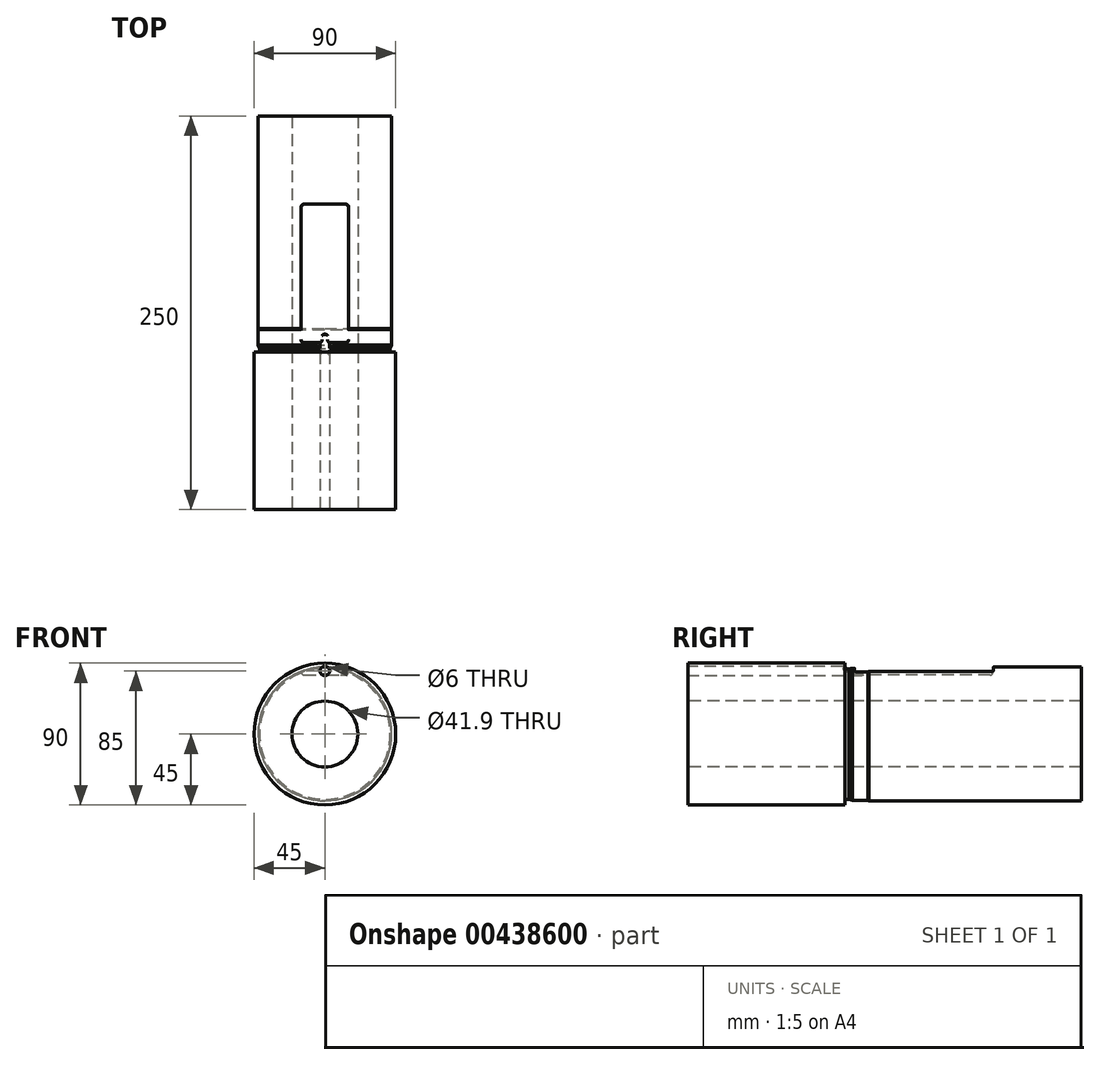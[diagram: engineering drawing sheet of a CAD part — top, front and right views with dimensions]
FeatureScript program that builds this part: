
annotation { "Feature Type Name" : "Feature", "Feature Type Description" : "" }
export const myFeature = defineFeature(function(context is Context, id is Id, definition is map)
    precondition{}
    {
        {
            var Q0;
            Q0=qCreatedBy(makeId("Right.planeOp"),FACE);
            var sketch = newSketch(context, id + "F0", { "sketchPlane" : qUnion([Q0])});
            skLineSegment(sketch, "E0", {"start": v(-100, 20.95) * mm, "end": v(-100, 45) * mm});
            skLineSegment(sketch, "E1", {"start": v(-100, 45) * mm, "end": v(0, 45) * mm});
            skLineSegment(sketch, "E2", {"start": v(0, 45) * mm, "end": v(0, 42.8) * mm});
            skArc(sketch, "E3", {"start": v(0, 42.8) * mm, "mid": v(0.38, 41.88) * mm, "end": v(1.3, 41.5) * mm});
            skLineSegment(sketch, "E4", {"start": v(4.63, 42.27) * mm, "end": v(14.4, 42.27) * mm});
            skLineSegment(sketch, "E5", {"start": v(14.4, 42.27) * mm, "end": v(15.2, 42.5) * mm});
            skLineSegment(sketch, "E6", {"start": v(15.2, 42.5) * mm, "end": v(150, 42.5) * mm});
            skLineSegment(sketch, "E7", {"start": v(150, 42.49) * mm, "end": v(150, 20.95) * mm});
            skLineSegment(sketch, "E8", {"start": v(-123.16, 0) * mm, "end": v(120.4, 0) * mm, "construction": true});
            skLineSegment(sketch, "E9", {"start": v(1.3, 41.5) * mm, "end": v(2.5, 41.5) * mm});
            skLineSegment(sketch, "E10", {"start": v(2.5, 41.5) * mm, "end": v(4.63, 42.27) * mm});
            skLineSegment(sketch, "E11", {"start": v(-100, 20.95) * mm, "end": v(150, 20.95) * mm});
            skSolve(sketch);
        }
        {
            var Q0;
            Q0=makeQuery(id+"F0.imprint","IMPRINT",FACE,{"disambiguationData":[TD([[makeQuery(id+"F0.imprint","IMPRINT",EDGE,{"derivedFrom":sQuery(id+"F0.wireOp",EDGE,"E0")}),-1.0]])]});
            var Q1;
            Q1=sQuery(id+"F0.wireOp",EDGE,"E8");
            revolve(context, id + "F1", {"entities" : qUnion([Q0]), "axis" : qUnion([Q1]), "revolveType" : RevolveType.FULL});
        }
        {
            var Q0;
            Q0=makeQuery(id+"F1.opRevolve","SWEPT_FACE",FACE,{"disambiguationData":[OSD([sQuery(id+"F0.wireOp",EDGE,"E0")])]});
            var sketch = newSketch(context, id + "F2", { "sketchPlane" : qUnion([Q0])});
            skCircle(sketch, "E12", {"center": v(0, 40) * mm, "radius": 3 * mm});
            skSolve(sketch);
        }
        {
            var Q0;
            Q0 = qSketchRegion(id + "F2", true);
            extrude(context, id + "F3", {"entities" : qUnion([Q0]), "operationType" : NewBodyOperationType.REMOVE, "oppositeDirection" : true, "depth" : 111.5 * mm, "offsetDistance" : 25 * mm});
        }
        {
            var Q0;
            Q0=qCreatedBy(makeId("Right.planeOp"),FACE);
            var sketch = newSketch(context, id + "F4", { "sketchPlane" : qUnion([Q0])});
            skLineSegment(sketch, "E13", {"start": v(94, 42.5) * mm, "end": v(94, 37.5) * mm});
            skLineSegment(sketch, "E14", {"start": v(94, 37.5) * mm, "end": v(6, 37.5) * mm});
            skLineSegment(sketch, "E15", {"start": v(6, 37.5) * mm, "end": v(6, 42.5) * mm});
            skLineSegment(sketch, "E16", {"start": v(6, 42.5) * mm, "end": v(94, 42.5) * mm});
            skSolve(sketch);
        }
        {
            var Q0;
            Q0 = qSketchRegion(id + "F4", true);
            extrude(context, id + "F5", {"entities" : qUnion([Q0]), "operationType" : NewBodyOperationType.REMOVE, "endBound" : BoundingType.SYMMETRIC, "oppositeDirection" : true, "depth" : 30 * mm, "offsetDistance" : 25 * mm});
        }
        {
            var Q0;
            Q0=qCreatedBy(makeId("Right.planeOp"),FACE);
            var sketch = newSketch(context, id + "F6", { "sketchPlane" : qUnion([Q0])});
            skLineSegment(sketch, "E17.bottom", {"start": v(2, 44.7) * mm, "end": v(8, 44.7) * mm});
            skLineSegment(sketch, "E17.top", {"start": v(2, 41.7) * mm, "end": v(8, 41.7) * mm});
            skLineSegment(sketch, "E17.left", {"start": v(2, 44.7) * mm, "end": v(2, 41.7) * mm});
            skLineSegment(sketch, "E17.right", {"start": v(8, 44.7) * mm, "end": v(8, 41.7) * mm});
            skSolve(sketch);
        }
        {
            var Q0;
            Q0 = qSketchRegion(id + "F6", true);
            extrude(context, id + "F7", {"entities" : qUnion([Q0]), "operationType" : NewBodyOperationType.REMOVE, "endBound" : BoundingType.SYMMETRIC, "oppositeDirection" : true, "depth" : 30 * mm, "offsetDistance" : 25 * mm});
        }
        {
            var Q0;
            Q0=makeQuery(id+"F5.boolean.opBoolean","COPY",EDGE,{"derivedFrom":makeQuery(id+"F5.opExtrude","CAP_EDGE",EDGE,{"disambiguationData":[OSD([sQuery(id+"F4.wireOp",EDGE,"E15")])],"isStart":false})});
            var Q1;
            Q1=makeQuery(id+"F5.boolean.opBoolean","COPY",EDGE,{"derivedFrom":makeQuery(id+"F5.opExtrude","CAP_EDGE",EDGE,{"disambiguationData":[OSD([sQuery(id+"F4.wireOp",EDGE,"E15")])],"isStart":true})});
            var Q2;
            Q2=makeQuery(id+"F5.boolean.opBoolean","COPY",EDGE,{"derivedFrom":makeQuery(id+"F5.opExtrude","CAP_EDGE",EDGE,{"disambiguationData":[OSD([sQuery(id+"F4.wireOp",EDGE,"E13")])],"isStart":true})});
            var Q3;
            Q3=makeQuery(id+"F5.boolean.opBoolean","COPY",EDGE,{"derivedFrom":makeQuery(id+"F5.opExtrude","CAP_EDGE",EDGE,{"disambiguationData":[OSD([sQuery(id+"F4.wireOp",EDGE,"E13")])],"isStart":false})});
            var Q4;
            Q4=makeQuery(id+"F5.boolean.opBoolean","COPY",EDGE,{"derivedFrom":makeQuery(id+"F5.opExtrude","SWEPT_EDGE",EDGE,{"disambiguationData":[OSD([sQuery(id+"F4.wireOp",EDGE,"E13"),sQuery(id+"F4.wireOp",EDGE,"E14")])]})});
            var Q5;
            Q5=makeQuery(id+"F5.boolean.opBoolean","COPY",EDGE,{"derivedFrom":makeQuery(id+"F5.opExtrude","CAP_EDGE",EDGE,{"disambiguationData":[OSD([sQuery(id+"F4.wireOp",EDGE,"E14")])],"isStart":false})});
            var Q6;
            Q6=makeQuery(id+"F5.boolean.opBoolean","COPY",EDGE,{"derivedFrom":makeQuery(id+"F5.opExtrude","CAP_EDGE",EDGE,{"disambiguationData":[OSD([sQuery(id+"F4.wireOp",EDGE,"E14")])],"isStart":true})});
            var Q7;
            {var subQ0=sQuery(id+"F4.wireOp",EDGE,"E15");var subQ1=sQuery(id+"F4.wireOp",EDGE,"E14");Q7=makeQuery(id+"F5.boolean.opBoolean","COPY",EDGE,{"disambiguationData":[TD([makeQuery(id+"F5.opExtrude","CAP_FACE",FACE,{"disambiguationData":[OSD([sQuery(id+"F4.wireOp",EDGE,"E13"),subQ1,subQ0,sQuery(id+"F4.wireOp",EDGE,"E16")])],"isStart":true})])],"derivedFrom":makeQuery(id+"F5.opExtrude","SWEPT_EDGE",EDGE,{"disambiguationData":[OSD([subQ1,subQ0])]})});}
            var Q8;
            {var subQ0=sQuery(id+"F4.wireOp",EDGE,"E15");var subQ1=sQuery(id+"F4.wireOp",EDGE,"E14");Q8=makeQuery(id+"F5.boolean.opBoolean","COPY",EDGE,{"disambiguationData":[TD([makeQuery(id+"F5.opExtrude","CAP_FACE",FACE,{"disambiguationData":[OSD([sQuery(id+"F4.wireOp",EDGE,"E13"),subQ1,subQ0,sQuery(id+"F4.wireOp",EDGE,"E16")])],"isStart":false})])],"derivedFrom":makeQuery(id+"F5.opExtrude","SWEPT_EDGE",EDGE,{"disambiguationData":[OSD([subQ1,subQ0])]})});}
            fillet(context, id + "F8", {"entities" : qUnion([Q0, Q1, Q2, Q3, Q4, Q5, Q6, Q7, Q8]), "radius" : 2 * mm, "tangentPropagation" : true, "allowEdgeOverflow" : false});
        }
        {
            var Q0;
            Q0=makeQuery(id+"F3.boolean.opBoolean","COPY",EDGE,{"derivedFrom":makeQuery(id+"F3.opExtrude","CAP_EDGE",EDGE,{"disambiguationData":[OSD([sQuery(id+"F2.wireOp",EDGE,"E12")])],"isStart":false})});
            fillet(context, id + "F9", {"entities" : qUnion([Q0]), "radius" : 1 * mm, "tangentPropagation" : true, "allowEdgeOverflow" : false});
        }
        {
            var Q0;
            Q0=makeQuery(id+"F5.boolean.opBoolean","INTERSECT",EDGE,{"disambiguationData":[OD(1.0)],"derivedFrom":[makeQuery(id+"F3.boolean.opBoolean","COPY",FACE,{"derivedFrom":makeQuery(id+"F3.opExtrude","SWEPT_FACE",FACE,{"disambiguationData":[OSD([sQuery(id+"F2.wireOp",EDGE,"E12")])]})}),makeQuery(id+"F5.opExtrude","SWEPT_FACE",FACE,{"disambiguationData":[OSD([sQuery(id+"F4.wireOp",EDGE,"E15")])]})]});
            fillet(context, id + "F10", {"entities" : qUnion([Q0]), "radius" : 0.15 * mm, "tangentPropagation" : true, "allowEdgeOverflow" : false});
        }
        {
            var Q0;
            Q0=makeQuery(id+"F3.boolean.opBoolean","INTERSECT",EDGE,{"disambiguationData":[OD(1.0)],"derivedFrom":[makeQuery(id+"F1.opRevolve","SWEPT_FACE",FACE,{"disambiguationData":[OSD([sQuery(id+"F0.wireOp",EDGE,"E3")])]}),makeQuery(id+"F3.opExtrude","SWEPT_FACE",FACE,{"disambiguationData":[OSD([sQuery(id+"F2.wireOp",EDGE,"E12")])]})]});
            var Q1;
            Q1=makeQuery(id+"F3.boolean.opBoolean","INTERSECT",EDGE,{"derivedFrom":[makeQuery(id+"F1.opRevolve","SWEPT_FACE",FACE,{"disambiguationData":[OSD([sQuery(id+"F0.wireOp",EDGE,"E2")])]}),makeQuery(id+"F3.opExtrude","SWEPT_FACE",FACE,{"disambiguationData":[OSD([sQuery(id+"F2.wireOp",EDGE,"E12")])]})]});
            var Q2;
            Q2=makeQuery(id+"F3.boolean.opBoolean","INTERSECT",EDGE,{"disambiguationData":[OD(0.0)],"derivedFrom":[makeQuery(id+"F1.opRevolve","SWEPT_FACE",FACE,{"disambiguationData":[OSD([sQuery(id+"F0.wireOp",EDGE,"E3")])]}),makeQuery(id+"F3.opExtrude","SWEPT_FACE",FACE,{"disambiguationData":[OSD([sQuery(id+"F2.wireOp",EDGE,"E12")])]})]});
            var Q3;
            Q3=makeQuery(id+"F3.boolean.opBoolean","INTERSECT",EDGE,{"disambiguationData":[OD(0.0)],"derivedFrom":[makeQuery(id+"F1.opRevolve","SWEPT_FACE",FACE,{"disambiguationData":[OSD([sQuery(id+"F0.wireOp",EDGE,"E9")])]}),makeQuery(id+"F3.opExtrude","SWEPT_FACE",FACE,{"disambiguationData":[OSD([sQuery(id+"F2.wireOp",EDGE,"E12")])]})]});
            var Q4;
            Q4=makeQuery(id+"F3.boolean.opBoolean","INTERSECT",EDGE,{"disambiguationData":[OD(0.0)],"derivedFrom":[makeQuery(id+"F1.opRevolve","SWEPT_FACE",FACE,{"disambiguationData":[OSD([sQuery(id+"F0.wireOp",EDGE,"E10")])]}),makeQuery(id+"F3.opExtrude","SWEPT_FACE",FACE,{"disambiguationData":[OSD([sQuery(id+"F2.wireOp",EDGE,"E12")])]})]});
            var Q5;
            Q5=makeQuery(id+"F7.boolean.opBoolean","INTERSECT",EDGE,{"disambiguationData":[OD(0.0)],"derivedFrom":[makeQuery(id+"F3.boolean.opBoolean","COPY",FACE,{"derivedFrom":makeQuery(id+"F3.opExtrude","SWEPT_FACE",FACE,{"disambiguationData":[OSD([sQuery(id+"F2.wireOp",EDGE,"E12")])]})}),makeQuery(id+"F7.opExtrude","SWEPT_FACE",FACE,{"disambiguationData":[OSD([sQuery(id+"F6.wireOp",EDGE,"E17.top")])]})]});
            var Q6;
            Q6=makeQuery(id+"F3.boolean.opBoolean","INTERSECT",EDGE,{"disambiguationData":[OD(1.0)],"derivedFrom":[makeQuery(id+"F1.opRevolve","SWEPT_FACE",FACE,{"disambiguationData":[OSD([sQuery(id+"F0.wireOp",EDGE,"E9")])]}),makeQuery(id+"F3.opExtrude","SWEPT_FACE",FACE,{"disambiguationData":[OSD([sQuery(id+"F2.wireOp",EDGE,"E12")])]})]});
            var Q7;
            Q7=makeQuery(id+"F3.boolean.opBoolean","INTERSECT",EDGE,{"disambiguationData":[OD(1.0)],"derivedFrom":[makeQuery(id+"F1.opRevolve","SWEPT_FACE",FACE,{"disambiguationData":[OSD([sQuery(id+"F0.wireOp",EDGE,"E10")])]}),makeQuery(id+"F3.opExtrude","SWEPT_FACE",FACE,{"disambiguationData":[OSD([sQuery(id+"F2.wireOp",EDGE,"E12")])]})]});
            var Q8;
            Q8=makeQuery(id+"F7.boolean.opBoolean","INTERSECT",EDGE,{"disambiguationData":[OD(1.0)],"derivedFrom":[makeQuery(id+"F3.boolean.opBoolean","COPY",FACE,{"derivedFrom":makeQuery(id+"F3.opExtrude","SWEPT_FACE",FACE,{"disambiguationData":[OSD([sQuery(id+"F2.wireOp",EDGE,"E12")])]})}),makeQuery(id+"F7.opExtrude","SWEPT_FACE",FACE,{"disambiguationData":[OSD([sQuery(id+"F6.wireOp",EDGE,"E17.top")])]})]});
            fillet(context, id + "F11", {"entities" : qUnion([Q0, Q1, Q2, Q3, Q4, Q5, Q6, Q7, Q8]), "radius" : 1.5 * mm, "allowEdgeOverflow" : false});
        }
        {
            var Q0;
            Q0=makeQuery(id+"F5.boolean.opBoolean","INTERSECT",EDGE,{"derivedFrom":[makeQuery(id+"F1.opRevolve","SWEPT_FACE",FACE,{"disambiguationData":[OSD([sQuery(id+"F0.wireOp",EDGE,"E6")])]}),makeQuery(id+"F5.opExtrude","CAP_FACE",FACE,{"disambiguationData":[OSD([sQuery(id+"F4.wireOp",EDGE,"E13"),sQuery(id+"F4.wireOp",EDGE,"E14"),sQuery(id+"F4.wireOp",EDGE,"E15"),sQuery(id+"F4.wireOp",EDGE,"E16")])],"isStart":false})]});
            var Q1;
            Q1=makeQuery(id+"F5.boolean.opBoolean","INTERSECT",EDGE,{"derivedFrom":[makeQuery(id+"F1.opRevolve","SWEPT_FACE",FACE,{"disambiguationData":[OSD([sQuery(id+"F0.wireOp",EDGE,"E5")])]}),makeQuery(id+"F5.opExtrude","CAP_FACE",FACE,{"disambiguationData":[OSD([sQuery(id+"F4.wireOp",EDGE,"E13"),sQuery(id+"F4.wireOp",EDGE,"E14"),sQuery(id+"F4.wireOp",EDGE,"E15"),sQuery(id+"F4.wireOp",EDGE,"E16")])],"isStart":true})]});
            var Q2;
            Q2=makeQuery(id+"F5.boolean.opBoolean","INTERSECT",EDGE,{"derivedFrom":[makeQuery(id+"F1.opRevolve","SWEPT_FACE",FACE,{"disambiguationData":[OSD([sQuery(id+"F0.wireOp",EDGE,"E4")])]}),makeQuery(id+"F5.opExtrude","CAP_FACE",FACE,{"disambiguationData":[OSD([sQuery(id+"F4.wireOp",EDGE,"E13"),sQuery(id+"F4.wireOp",EDGE,"E14"),sQuery(id+"F4.wireOp",EDGE,"E15"),sQuery(id+"F4.wireOp",EDGE,"E16")])],"isStart":true})]});
            var Q3;
            {var subQ0=sQuery(id+"F4.wireOp",EDGE,"E15");var subQ1=sQuery(id+"F4.wireOp",EDGE,"E14");Q3=makeQuery(id+"F7.boolean.opBoolean","INTERSECT",EDGE,{"derivedFrom":[makeQuery(id+"F5.boolean.opBoolean","COPY",FACE,{"disambiguationData":[TD([makeQuery(id+"F5.opExtrude","CAP_FACE",FACE,{"disambiguationData":[OSD([sQuery(id+"F4.wireOp",EDGE,"E13"),subQ1,subQ0,sQuery(id+"F4.wireOp",EDGE,"E16")])],"isStart":true})])],"derivedFrom":makeQuery(id+"F5.opExtrude","SWEPT_FACE",FACE,{"disambiguationData":[OSD([subQ0])]})}),makeQuery(id+"F7.opExtrude","SWEPT_FACE",FACE,{"disambiguationData":[OSD([sQuery(id+"F6.wireOp",EDGE,"E17.top")])]})]});}
            var Q4;
            {var subQ0=makeQuery(id+"F3.boolean.opBoolean","COPY",FACE,{"derivedFrom":makeQuery(id+"F3.opExtrude","SWEPT_FACE",FACE,{"disambiguationData":[OSD([sQuery(id+"F2.wireOp",EDGE,"E12")])]})});var subQ1=sQuery(id+"F4.wireOp",EDGE,"E15");var subQ2=sQuery(id+"F4.wireOp",EDGE,"E14");Q4=makeQuery(id+"F11.opFillet","BLEND_EDGE",EDGE,{"blendedFrom":[makeQuery(id+"F7.boolean.opBoolean","INTERSECT",EDGE,{"disambiguationData":[OD(0.0)],"derivedFrom":[subQ0,makeQuery(id+"F7.opExtrude","SWEPT_FACE",FACE,{"disambiguationData":[OSD([sQuery(id+"F6.wireOp",EDGE,"E17.top")])]})]}),makeQuery(id+"F5.boolean.opBoolean","COPY",FACE,{"disambiguationData":[TD([makeQuery(id+"F5.opExtrude","CAP_FACE",FACE,{"disambiguationData":[OSD([sQuery(id+"F4.wireOp",EDGE,"E13"),subQ2,subQ1,sQuery(id+"F4.wireOp",EDGE,"E16")])],"isStart":false})])],"derivedFrom":makeQuery(id+"F5.opExtrude","SWEPT_FACE",FACE,{"disambiguationData":[OSD([subQ1])]})})],"blendedInto":[makeQuery(id+"F5.boolean.opBoolean","COPY",FACE,{"disambiguationData":[TD([makeQuery(id+"F5.opExtrude","CAP_FACE",FACE,{"disambiguationData":[OSD([sQuery(id+"F4.wireOp",EDGE,"E13"),subQ2,subQ1,sQuery(id+"F4.wireOp",EDGE,"E16")])],"isStart":false})])],"derivedFrom":makeQuery(id+"F5.opExtrude","SWEPT_FACE",FACE,{"disambiguationData":[OSD([subQ1])]})})]});}
            var Q5;
            Q5=makeQuery(id+"F5.boolean.opBoolean","INTERSECT",EDGE,{"disambiguationData":[OD(1.0)],"derivedFrom":[makeQuery(id+"F1.opRevolve","SWEPT_FACE",FACE,{"disambiguationData":[OSD([sQuery(id+"F0.wireOp",EDGE,"E4")])]}),makeQuery(id+"F5.opExtrude","SWEPT_FACE",FACE,{"disambiguationData":[OSD([sQuery(id+"F4.wireOp",EDGE,"E15")])]})]});
            fillet(context, id + "F12", {"entities" : qUnion([Q0, Q1, Q2, Q3, Q4, Q5]), "radius" : 0.15 * mm, "tangentPropagation" : true, "allowEdgeOverflow" : false});
        }
    });
